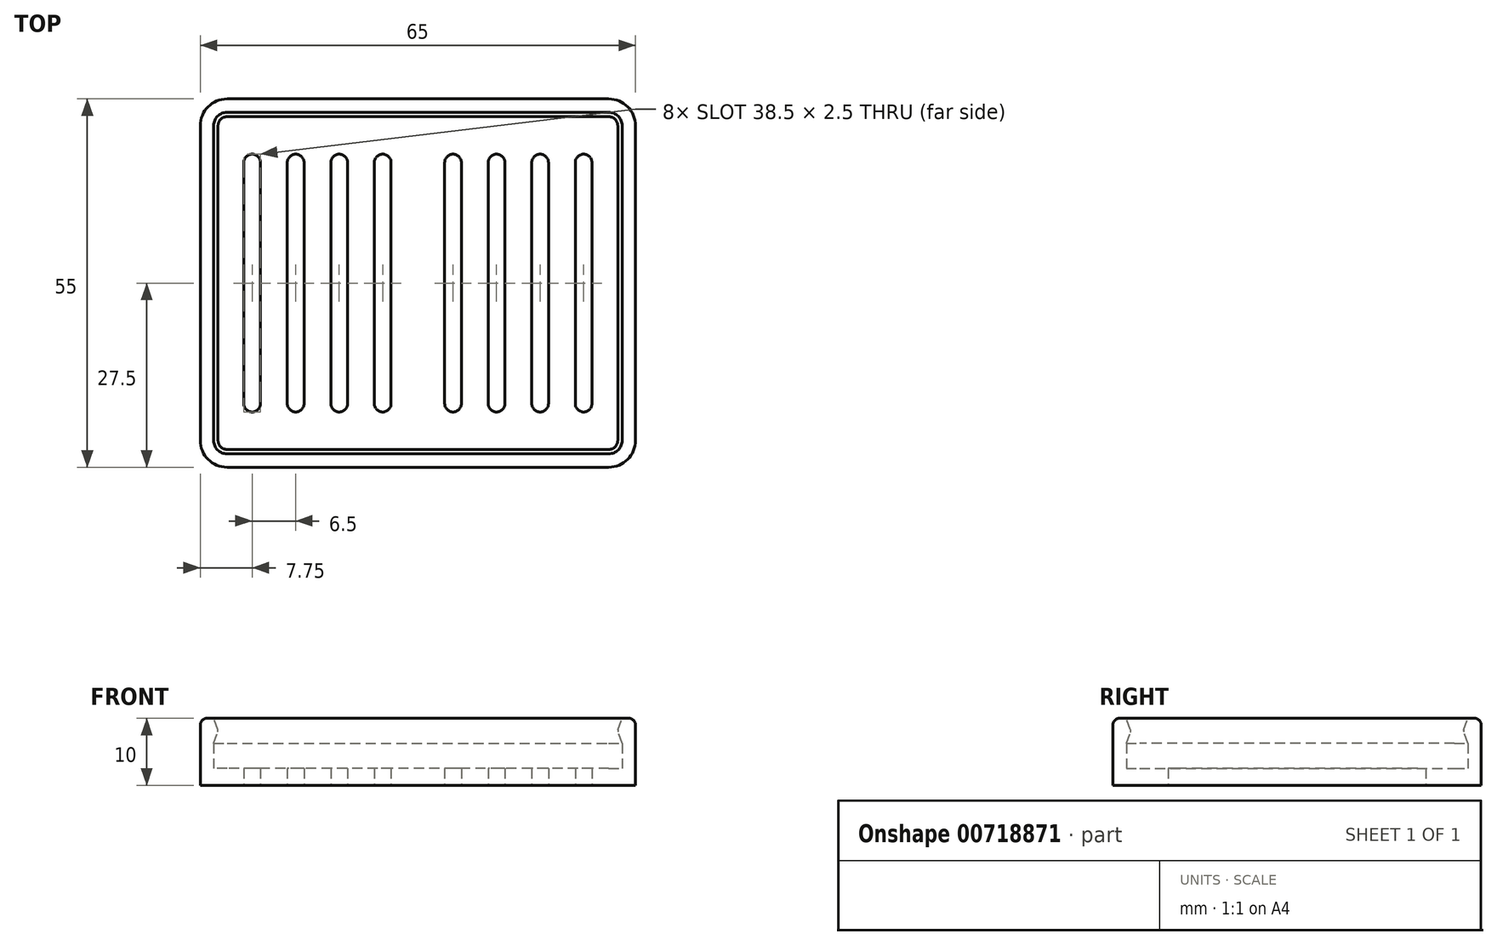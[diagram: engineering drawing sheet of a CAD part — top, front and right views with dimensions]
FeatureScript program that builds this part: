
annotation { "Feature Type Name" : "Feature", "Feature Type Description" : "" }
export const myFeature = defineFeature(function(context is Context, id is Id, definition is map)
    precondition{}
    {
        {
            var Q0;
            Q0=qCreatedBy(makeId("Top.planeOp"),FACE);
            var sketch = newSketch(context, id + "F0", { "sketchPlane" : qUnion([Q0])});
            skLineSegment(sketch, "E0.bottom", {"start": v(-32.5, 27.5) * mm, "end": v(32.5, 27.5) * mm});
            skLineSegment(sketch, "E0.top", {"start": v(-32.5, -27.5) * mm, "end": v(32.5, -27.5) * mm});
            skLineSegment(sketch, "E0.left", {"start": v(-32.5, 27.5) * mm, "end": v(-32.5, -27.5) * mm});
            skLineSegment(sketch, "E0.right", {"start": v(32.5, 27.5) * mm, "end": v(32.5, -27.5) * mm});
            skLineSegment(sketch, "E1.bottom", {"start": v(-30.5, 25.5) * mm, "end": v(30.5, 25.5) * mm});
            skLineSegment(sketch, "E1.top", {"start": v(-30.5, -25.5) * mm, "end": v(30.5, -25.5) * mm});
            skLineSegment(sketch, "E1.left", {"start": v(-30.5, 25.5) * mm, "end": v(-30.5, -25.5) * mm});
            skLineSegment(sketch, "E1.right", {"start": v(30.5, 25.5) * mm, "end": v(30.5, -25.5) * mm});
            skArc(sketch, "E2", {"start": v(-23.5, 18) * mm, "mid": v(-24.75, 19.25) * mm, "end": v(-26, 18) * mm});
            skArc(sketch, "E3.MirrorC", {"start": v(-23.5, -18) * mm, "mid": v(-24.75, -19.25) * mm, "end": v(-26, -18) * mm});
            skLineSegment(sketch, "E4", {"start": v(-26, 18) * mm, "end": v(-26, -18) * mm});
            skLineSegment(sketch, "E5", {"start": v(-23.5, 18) * mm, "end": v(-23.5, -18) * mm});
            skLineSegment(sketch, "E6.1.0.0", {"start": v(-19.5, 18) * mm, "end": v(-19.5, -18) * mm});
            skLineSegment(sketch, "E6.1.0.1", {"start": v(-17, 18) * mm, "end": v(-17, -18) * mm});
            skArc(sketch, "E6.1.0.2", {"start": v(-17, 18) * mm, "mid": v(-18.25, 19.25) * mm, "end": v(-19.5, 18) * mm});
            skArc(sketch, "E6.1.0.3", {"start": v(-17, -18) * mm, "mid": v(-18.25, -19.25) * mm, "end": v(-19.5, -18) * mm});
            skLineSegment(sketch, "E6.2.0.0", {"start": v(-13, 18) * mm, "end": v(-13, -18) * mm});
            skLineSegment(sketch, "E6.2.0.1", {"start": v(-10.5, 18) * mm, "end": v(-10.5, -18) * mm});
            skArc(sketch, "E6.2.0.2", {"start": v(-10.5, 18) * mm, "mid": v(-11.75, 19.25) * mm, "end": v(-13, 18) * mm});
            skArc(sketch, "E6.2.0.3", {"start": v(-10.5, -18) * mm, "mid": v(-11.75, -19.25) * mm, "end": v(-13, -18) * mm});
            skLineSegment(sketch, "E6.3.0.0", {"start": v(-6.5, 18) * mm, "end": v(-6.5, -18) * mm});
            skLineSegment(sketch, "E6.3.0.1", {"start": v(-4, 18) * mm, "end": v(-4, -18) * mm});
            skArc(sketch, "E6.3.0.2", {"start": v(-4, 18) * mm, "mid": v(-5.25, 19.25) * mm, "end": v(-6.5, 18) * mm});
            skArc(sketch, "E6.3.0.3", {"start": v(-4, -18) * mm, "mid": v(-5.25, -19.25) * mm, "end": v(-6.5, -18) * mm});
            skLineSegment(sketch, "E6.direction1", {"start": v(-26, -18) * mm, "end": v(-19.5, -18) * mm, "construction": true});
            skLineSegment(sketch, "E7.MirrorCS", {"start": v(4, 18) * mm, "end": v(4, -18) * mm});
            skLineSegment(sketch, "E8.MirrorCS", {"start": v(6.5, 18) * mm, "end": v(6.5, -18) * mm});
            skLineSegment(sketch, "E9.MirrorCS", {"start": v(10.5, 18) * mm, "end": v(10.5, -18) * mm});
            skLineSegment(sketch, "E10.MirrorCS", {"start": v(13, 18) * mm, "end": v(13, -18) * mm});
            skLineSegment(sketch, "E11.MirrorCS", {"start": v(19.5, 18) * mm, "end": v(19.5, -18) * mm});
            skLineSegment(sketch, "E12.MirrorCS", {"start": v(23.5, 18) * mm, "end": v(23.5, -18) * mm});
            skLineSegment(sketch, "E13.MirrorCS", {"start": v(26, 18) * mm, "end": v(26, -18) * mm});
            skLineSegment(sketch, "E14.MirrorCS", {"start": v(17, 18) * mm, "end": v(17, -18) * mm});
            skArc(sketch, "E15.MirrorCS", {"start": v(23.5, 18) * mm, "mid": v(24.75, 19.25) * mm, "end": v(26, 18) * mm});
            skArc(sketch, "E16.MirrorCS", {"start": v(17, 18) * mm, "mid": v(18.25, 19.25) * mm, "end": v(19.5, 18) * mm});
            skArc(sketch, "E17.MirrorCS", {"start": v(10.5, 18) * mm, "mid": v(11.75, 19.25) * mm, "end": v(13, 18) * mm});
            skArc(sketch, "E18.MirrorCS", {"start": v(4, 18) * mm, "mid": v(5.25, 19.25) * mm, "end": v(6.5, 18) * mm});
            skArc(sketch, "E19.MirrorCS", {"start": v(4, -18) * mm, "mid": v(5.25, -19.25) * mm, "end": v(6.5, -18) * mm});
            skArc(sketch, "E20.MirrorCS", {"start": v(10.5, -18) * mm, "mid": v(11.75, -19.25) * mm, "end": v(13, -18) * mm});
            skArc(sketch, "E21.MirrorCS", {"start": v(17, -18) * mm, "mid": v(18.25, -19.25) * mm, "end": v(19.5, -18) * mm});
            skArc(sketch, "E22.MirrorCS", {"start": v(23.5, -18) * mm, "mid": v(24.75, -19.25) * mm, "end": v(26, -18) * mm});
            skSolve(sketch);
        }
        {
            var Q0;
            Q0=makeQuery(id+"F0.imprint","IMPRINT",FACE,{"disambiguationData":[TD([[makeQuery(id+"F0.imprint","IMPRINT",EDGE,{"derivedFrom":sQuery(id+"F0.wireOp",EDGE,"E1.bottom")}),-1.0]])]});
            var Q1;
            Q1=makeQuery(id+"F0.imprint","IMPRINT",FACE,{"disambiguationData":[TD([[makeQuery(id+"F0.imprint","IMPRINT",EDGE,{"derivedFrom":sQuery(id+"F0.wireOp",EDGE,"E0.bottom")}),-1.0]])]});
            extrude(context, id + "F1", {"entities" : qUnion([Q0, Q1]), "depth" : 2.5 * mm, "offsetDistance" : 25 * mm});
        }
        {
            var Q0;
            Q0=makeQuery(id+"F0.imprint","IMPRINT",FACE,{"disambiguationData":[TD([[makeQuery(id+"F0.imprint","IMPRINT",EDGE,{"derivedFrom":sQuery(id+"F0.wireOp",EDGE,"E0.bottom")}),-1.0]])]});
            extrude(context, id + "F2", {"entities" : qUnion([Q0]), "operationType" : NewBodyOperationType.ADD, "depth" : 10 * mm, "offsetDistance" : 25 * mm});
        }
        {
            var Q0;
            Q0=makeQuery(id+"F2.opExtrude","SWEPT_EDGE",EDGE,{"disambiguationData":[OSD([sQuery(id+"F0.wireOp",EDGE,"E1.bottom"),sQuery(id+"F0.wireOp",EDGE,"E1.left")])]});
            var Q1;
            Q1=makeQuery(id+"F2.opExtrude","SWEPT_EDGE",EDGE,{"disambiguationData":[OSD([sQuery(id+"F0.wireOp",EDGE,"E1.bottom"),sQuery(id+"F0.wireOp",EDGE,"E1.right")])]});
            var Q2;
            Q2=makeQuery(id+"F2.opExtrude","SWEPT_EDGE",EDGE,{"disambiguationData":[OSD([sQuery(id+"F0.wireOp",EDGE,"E1.top"),sQuery(id+"F0.wireOp",EDGE,"E1.left")])]});
            var Q3;
            Q3=makeQuery(id+"F2.opExtrude","SWEPT_EDGE",EDGE,{"disambiguationData":[OSD([sQuery(id+"F0.wireOp",EDGE,"E1.top"),sQuery(id+"F0.wireOp",EDGE,"E1.right")])]});
            fillet(context, id + "F3", {"entities" : qUnion([Q0, Q1, Q2, Q3]), "radius" : 2 * mm, "tangentPropagation" : true, "allowEdgeOverflow" : false});
        }
        {
            var Q0;
            {var subQ0=sQuery(id+"F0.wireOp",EDGE,"E0.left");var subQ1=sQuery(id+"F0.wireOp",EDGE,"E0.bottom");Q0=makeQuery(id+"F2.boolean.opBoolean","MERGE",EDGE,{"derivedFrom":[makeQuery(id+"F1.opExtrude","SWEPT_EDGE",EDGE,{"disambiguationData":[OSD([subQ1,subQ0])]}),makeQuery(id+"F2.opExtrude","SWEPT_EDGE",EDGE,{"disambiguationData":[OSD([subQ1,subQ0])]})]});}
            var Q1;
            {var subQ0=sQuery(id+"F0.wireOp",EDGE,"E0.right");var subQ1=sQuery(id+"F0.wireOp",EDGE,"E0.bottom");Q1=makeQuery(id+"F2.boolean.opBoolean","MERGE",EDGE,{"derivedFrom":[makeQuery(id+"F1.opExtrude","SWEPT_EDGE",EDGE,{"disambiguationData":[OSD([subQ1,subQ0])]}),makeQuery(id+"F2.opExtrude","SWEPT_EDGE",EDGE,{"disambiguationData":[OSD([subQ1,subQ0])]})]});}
            var Q2;
            {var subQ0=sQuery(id+"F0.wireOp",EDGE,"E0.left");var subQ1=sQuery(id+"F0.wireOp",EDGE,"E0.top");Q2=makeQuery(id+"F2.boolean.opBoolean","MERGE",EDGE,{"derivedFrom":[makeQuery(id+"F1.opExtrude","SWEPT_EDGE",EDGE,{"disambiguationData":[OSD([subQ1,subQ0])]}),makeQuery(id+"F2.opExtrude","SWEPT_EDGE",EDGE,{"disambiguationData":[OSD([subQ1,subQ0])]})]});}
            var Q3;
            {var subQ0=sQuery(id+"F0.wireOp",EDGE,"E0.right");var subQ1=sQuery(id+"F0.wireOp",EDGE,"E0.top");Q3=makeQuery(id+"F2.boolean.opBoolean","MERGE",EDGE,{"derivedFrom":[makeQuery(id+"F1.opExtrude","SWEPT_EDGE",EDGE,{"disambiguationData":[OSD([subQ1,subQ0])]}),makeQuery(id+"F2.opExtrude","SWEPT_EDGE",EDGE,{"disambiguationData":[OSD([subQ1,subQ0])]})]});}
            fillet(context, id + "F4", {"entities" : qUnion([Q0, Q1, Q2, Q3]), "radius" : 4 * mm, "tangentPropagation" : true, "allowEdgeOverflow" : false});
        }
        {
            var Q0;
            Q0=qCreatedBy(makeId("Front.planeOp"),FACE);
            var sketch = newSketch(context, id + "F5", { "sketchPlane" : qUnion([Q0])});
            skLineSegment(sketch, "E23", {"start": v(-30.5, 6.25) * mm, "end": v(-29.88, 7.96) * mm});
            skLineSegment(sketch, "E24", {"start": v(-29.88, 8.3) * mm, "end": v(-30.5, 10) * mm});
            skLineSegment(sketch, "E25", {"start": v(-30.5, 6.25) * mm, "end": v(-30.5, 10) * mm});
            skArc(sketch, "E26", {"start": v(-29.88, 7.96) * mm, "mid": v(-29.85, 8.13) * mm, "end": v(-29.88, 8.3) * mm});
            skSolve(sketch);
        }
        {
            var Q0;
            Q0=makeQuery(id+"F5.imprint","IMPRINT",FACE,{"disambiguationData":[TD([[makeQuery(id+"F5.imprint","IMPRINT",EDGE,{"derivedFrom":sQuery(id+"F5.wireOp",EDGE,"E23")}),1.0]])]});
            var Q1;
            Q1=makeQuery(id+"F2.opExtrude","CAP_EDGE",EDGE,{"disambiguationData":[OSD([sQuery(id+"F0.wireOp",EDGE,"E1.left")])],"isStart":false});
            var Q2;
            {var subQ0=sQuery(id+"F0.wireOp",EDGE,"E1.left");var subQ1=sQuery(id+"F0.wireOp",EDGE,"E1.bottom");Q2=makeQuery(id+"F3.opFillet","BLEND_EDGE",EDGE,{"blendedFrom":[makeQuery(id+"F2.opExtrude","SWEPT_EDGE",EDGE,{"disambiguationData":[OSD([subQ1,subQ0])]}),makeQuery(id+"F2.opExtrude","CAP_FACE",FACE,{"disambiguationData":[OSD([sQuery(id+"F0.wireOp",EDGE,"E0.bottom"),sQuery(id+"F0.wireOp",EDGE,"E0.top"),sQuery(id+"F0.wireOp",EDGE,"E0.left"),sQuery(id+"F0.wireOp",EDGE,"E0.right"),subQ1,sQuery(id+"F0.wireOp",EDGE,"E1.top"),subQ0,sQuery(id+"F0.wireOp",EDGE,"E1.right")])],"isStart":false})],"blendedInto":[makeQuery(id+"F2.opExtrude","CAP_FACE",FACE,{"disambiguationData":[OSD([sQuery(id+"F0.wireOp",EDGE,"E0.bottom"),sQuery(id+"F0.wireOp",EDGE,"E0.top"),sQuery(id+"F0.wireOp",EDGE,"E0.left"),sQuery(id+"F0.wireOp",EDGE,"E0.right"),subQ1,sQuery(id+"F0.wireOp",EDGE,"E1.top"),subQ0,sQuery(id+"F0.wireOp",EDGE,"E1.right")])],"isStart":false})]});}
            var Q3;
            Q3=makeQuery(id+"F2.opExtrude","CAP_EDGE",EDGE,{"disambiguationData":[OSD([sQuery(id+"F0.wireOp",EDGE,"E1.bottom")])],"isStart":false});
            var Q4;
            {var subQ0=sQuery(id+"F0.wireOp",EDGE,"E1.left");var subQ1=sQuery(id+"F0.wireOp",EDGE,"E1.top");Q4=makeQuery(id+"F3.opFillet","BLEND_EDGE",EDGE,{"blendedFrom":[makeQuery(id+"F2.opExtrude","SWEPT_EDGE",EDGE,{"disambiguationData":[OSD([subQ1,subQ0])]}),makeQuery(id+"F2.opExtrude","CAP_FACE",FACE,{"disambiguationData":[OSD([sQuery(id+"F0.wireOp",EDGE,"E0.bottom"),sQuery(id+"F0.wireOp",EDGE,"E0.top"),sQuery(id+"F0.wireOp",EDGE,"E0.left"),sQuery(id+"F0.wireOp",EDGE,"E0.right"),sQuery(id+"F0.wireOp",EDGE,"E1.bottom"),subQ1,subQ0,sQuery(id+"F0.wireOp",EDGE,"E1.right")])],"isStart":false})],"blendedInto":[makeQuery(id+"F2.opExtrude","CAP_FACE",FACE,{"disambiguationData":[OSD([sQuery(id+"F0.wireOp",EDGE,"E0.bottom"),sQuery(id+"F0.wireOp",EDGE,"E0.top"),sQuery(id+"F0.wireOp",EDGE,"E0.left"),sQuery(id+"F0.wireOp",EDGE,"E0.right"),sQuery(id+"F0.wireOp",EDGE,"E1.bottom"),subQ1,subQ0,sQuery(id+"F0.wireOp",EDGE,"E1.right")])],"isStart":false})]});}
            var Q5;
            Q5=makeQuery(id+"F2.opExtrude","CAP_EDGE",EDGE,{"disambiguationData":[OSD([sQuery(id+"F0.wireOp",EDGE,"E1.top")])],"isStart":false});
            var Q6;
            {var subQ0=sQuery(id+"F0.wireOp",EDGE,"E1.right");var subQ1=sQuery(id+"F0.wireOp",EDGE,"E1.top");Q6=makeQuery(id+"F3.opFillet","BLEND_EDGE",EDGE,{"blendedFrom":[makeQuery(id+"F2.opExtrude","SWEPT_EDGE",EDGE,{"disambiguationData":[OSD([subQ1,subQ0])]}),makeQuery(id+"F2.opExtrude","CAP_FACE",FACE,{"disambiguationData":[OSD([sQuery(id+"F0.wireOp",EDGE,"E0.bottom"),sQuery(id+"F0.wireOp",EDGE,"E0.top"),sQuery(id+"F0.wireOp",EDGE,"E0.left"),sQuery(id+"F0.wireOp",EDGE,"E0.right"),sQuery(id+"F0.wireOp",EDGE,"E1.bottom"),subQ1,sQuery(id+"F0.wireOp",EDGE,"E1.left"),subQ0])],"isStart":false})],"blendedInto":[makeQuery(id+"F2.opExtrude","CAP_FACE",FACE,{"disambiguationData":[OSD([sQuery(id+"F0.wireOp",EDGE,"E0.bottom"),sQuery(id+"F0.wireOp",EDGE,"E0.top"),sQuery(id+"F0.wireOp",EDGE,"E0.left"),sQuery(id+"F0.wireOp",EDGE,"E0.right"),sQuery(id+"F0.wireOp",EDGE,"E1.bottom"),subQ1,sQuery(id+"F0.wireOp",EDGE,"E1.left"),subQ0])],"isStart":false})]});}
            var Q7;
            {var subQ0=sQuery(id+"F0.wireOp",EDGE,"E1.right");var subQ1=sQuery(id+"F0.wireOp",EDGE,"E1.bottom");Q7=makeQuery(id+"F3.opFillet","BLEND_EDGE",EDGE,{"blendedFrom":[makeQuery(id+"F2.opExtrude","SWEPT_EDGE",EDGE,{"disambiguationData":[OSD([subQ1,subQ0])]}),makeQuery(id+"F2.opExtrude","CAP_FACE",FACE,{"disambiguationData":[OSD([sQuery(id+"F0.wireOp",EDGE,"E0.bottom"),sQuery(id+"F0.wireOp",EDGE,"E0.top"),sQuery(id+"F0.wireOp",EDGE,"E0.left"),sQuery(id+"F0.wireOp",EDGE,"E0.right"),subQ1,sQuery(id+"F0.wireOp",EDGE,"E1.top"),sQuery(id+"F0.wireOp",EDGE,"E1.left"),subQ0])],"isStart":false})],"blendedInto":[makeQuery(id+"F2.opExtrude","CAP_FACE",FACE,{"disambiguationData":[OSD([sQuery(id+"F0.wireOp",EDGE,"E0.bottom"),sQuery(id+"F0.wireOp",EDGE,"E0.top"),sQuery(id+"F0.wireOp",EDGE,"E0.left"),sQuery(id+"F0.wireOp",EDGE,"E0.right"),subQ1,sQuery(id+"F0.wireOp",EDGE,"E1.top"),sQuery(id+"F0.wireOp",EDGE,"E1.left"),subQ0])],"isStart":false})]});}
            var Q8;
            Q8=makeQuery(id+"F2.opExtrude","CAP_EDGE",EDGE,{"disambiguationData":[OSD([sQuery(id+"F0.wireOp",EDGE,"E1.right")])],"isStart":false});
            sweep(context, id + "F6", {"operationType" : NewBodyOperationType.ADD, "profiles" : qUnion([Q0]), "path" : qUnion([Q1, Q2, Q3, Q4, Q5, Q6, Q7, Q8])});
        }
        {
            var Q0;
            Q0=makeQuery(id+"F2.opExtrude","CAP_EDGE",EDGE,{"disambiguationData":[OSD([sQuery(id+"F0.wireOp",EDGE,"E0.bottom")])],"isStart":false});
            fillet(context, id + "F7", {"entities" : qUnion([Q0]), "radius" : 1 * mm, "tangentPropagation" : true, "allowEdgeOverflow" : false});
        }
    });
